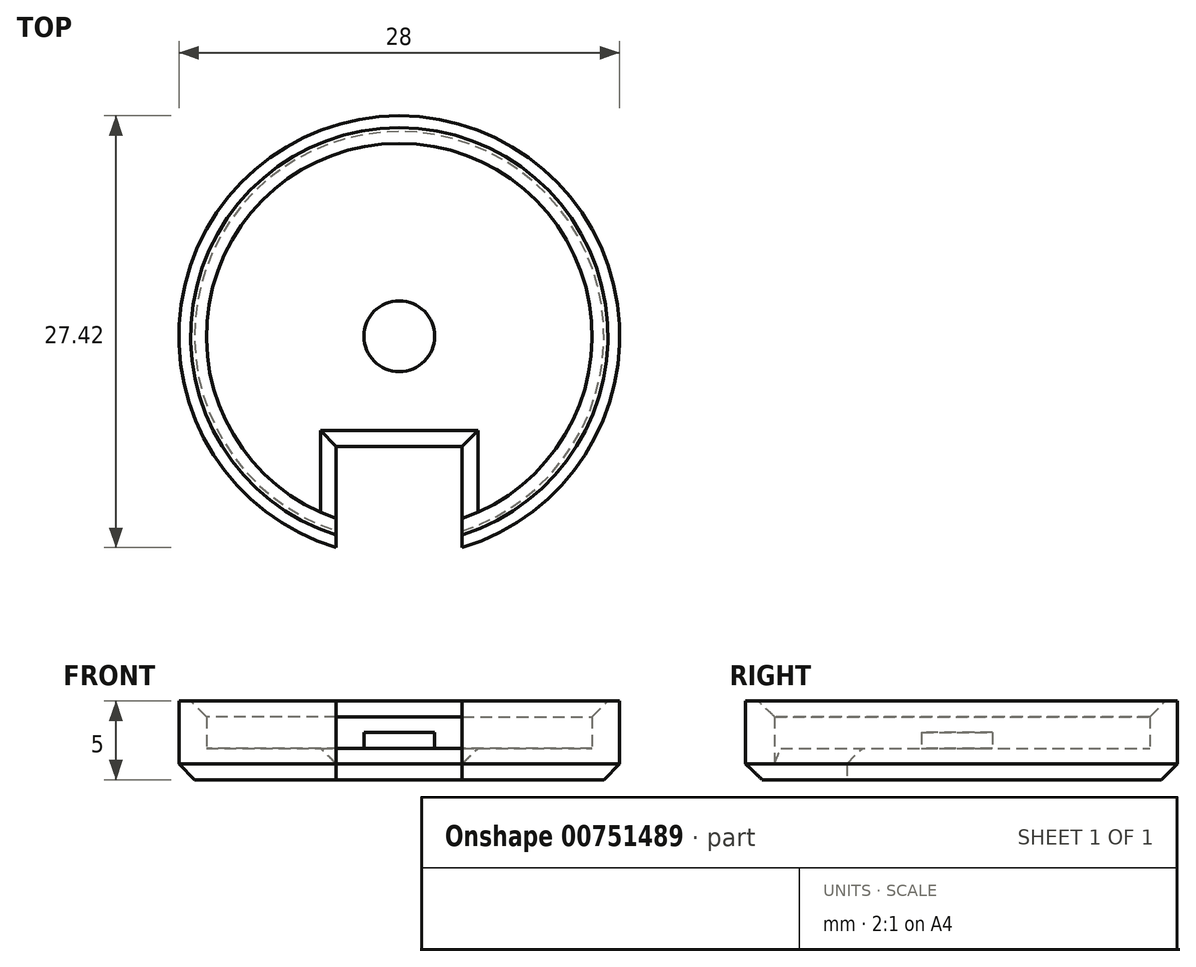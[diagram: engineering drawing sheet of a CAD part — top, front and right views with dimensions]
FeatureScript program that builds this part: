
annotation { "Feature Type Name" : "Feature", "Feature Type Description" : "" }
export const myFeature = defineFeature(function(context is Context, id is Id, definition is map)
    precondition{}
    {
        {
            var Q0;
            Q0=qCreatedBy(makeId("Top.planeOp"),FACE);
            var sketch = newSketch(context, id + "F0", { "sketchPlane" : qUnion([Q0])});
            skCircle(sketch, "E0", {"center": v(0, 0) * mm, "radius": 14 * mm});
            skCircle(sketch, "E1", {"center": v(0, 0) * mm, "radius": 2.25 * mm});
            skCircle(sketch, "E2", {"center": v(0, 0) * mm, "radius": 12.25 * mm});
            skLineSegment(sketch, "E3.bottom", {"start": v(-4, -7) * mm, "end": v(4, -7) * mm});
            skLineSegment(sketch, "E3.top", {"start": v(-4, -17.1) * mm, "end": v(4, -17.1) * mm});
            skLineSegment(sketch, "E3.left", {"start": v(-4, -7) * mm, "end": v(-4, -17.1) * mm});
            skLineSegment(sketch, "E3.right", {"start": v(4, -7) * mm, "end": v(4, -17.1) * mm});
            skSolve(sketch);
        }
        {
            var Q0;
            {var subQ0=sQuery(id+"F0.wireOp",EDGE,"E3.left");var subQ1=sQuery(id+"F0.wireOp",EDGE,"E0");var subQ2=makeQuery(id+"F0.imprint","INTERSECT",VERTEX,{"derivedFrom":[subQ1,subQ0]});Q0=makeQuery(id+"F0.imprint","IMPRINT",FACE,{"disambiguationData":[TD([[makeQuery(id+"F0.imprint","IMPRINT",EDGE,{"disambiguationData":[TD([[subQ2,1.0]])],"derivedFrom":subQ1}),1.0]])]});}
            var Q1;
            Q1=makeQuery(id+"F0.imprint","IMPRINT",FACE,{"disambiguationData":[TD([[makeQuery(id+"F0.imprint","IMPRINT",EDGE,{"derivedFrom":sQuery(id+"F0.wireOp",EDGE,"E1")}),-1.0]])]});
            var Q2;
            Q2=makeQuery(id+"F0.imprint","IMPRINT",FACE,{"disambiguationData":[TD([[makeQuery(id+"F0.imprint","IMPRINT",EDGE,{"derivedFrom":sQuery(id+"F0.wireOp",EDGE,"E1")}),1.0]])]});
            extrude(context, id + "F1", {"entities" : qUnion([Q0, Q1, Q2]), "depth" : 2 * mm, "offsetDistance" : 25 * mm});
        }
        {
            var Q0;
            {var subQ0=sQuery(id+"F0.wireOp",EDGE,"E3.left");var subQ1=sQuery(id+"F0.wireOp",EDGE,"E0");var subQ2=makeQuery(id+"F0.imprint","INTERSECT",VERTEX,{"derivedFrom":[subQ1,subQ0]});Q0=makeQuery(id+"F0.imprint","IMPRINT",FACE,{"disambiguationData":[TD([[makeQuery(id+"F0.imprint","IMPRINT",EDGE,{"disambiguationData":[TD([[subQ2,1.0]])],"derivedFrom":subQ1}),1.0]])]});}
            extrude(context, id + "F2", {"entities" : qUnion([Q0]), "operationType" : NewBodyOperationType.ADD, "depth" : 5 * mm, "offsetDistance" : 25 * mm});
        }
        {
            var Q0;
            Q0=makeQuery(id+"F0.imprint","IMPRINT",FACE,{"disambiguationData":[TD([[makeQuery(id+"F0.imprint","IMPRINT",EDGE,{"derivedFrom":sQuery(id+"F0.wireOp",EDGE,"E1")}),1.0]])]});
            extrude(context, id + "F3", {"entities" : qUnion([Q0]), "operationType" : NewBodyOperationType.ADD, "depth" : 3 * mm, "offsetDistance" : 25 * mm});
        }
        {
            var Q0;
            Q0=makeQuery(id+"F1.opExtrude","CAP_EDGE",EDGE,{"disambiguationData":[OSD([sQuery(id+"F0.wireOp",EDGE,"E0")])],"isStart":true});
            var Q1;
            Q1=makeQuery(id+"F2.opExtrude","CAP_EDGE",EDGE,{"disambiguationData":[OSD([sQuery(id+"F0.wireOp",EDGE,"E2")])],"isStart":false});
            var Q2;
            Q2=makeQuery(id+"F1.opExtrude","CAP_EDGE",EDGE,{"disambiguationData":[OSD([sQuery(id+"F0.wireOp",EDGE,"E3.bottom")])],"isStart":false});
            var Q3;
            Q3=makeQuery(id+"F1.opExtrude","CAP_EDGE",EDGE,{"disambiguationData":[OSD([sQuery(id+"F0.wireOp",EDGE,"E3.left")])],"isStart":false});
            var Q4;
            Q4=makeQuery(id+"F1.opExtrude","CAP_EDGE",EDGE,{"disambiguationData":[OSD([sQuery(id+"F0.wireOp",EDGE,"E3.right")])],"isStart":false});
            chamfer(context, id + "F4", {"entities" : qUnion([Q0, Q1, Q2, Q3, Q4]), "width" : 1 * mm, "tangentPropagation" : true});
        }
    });
